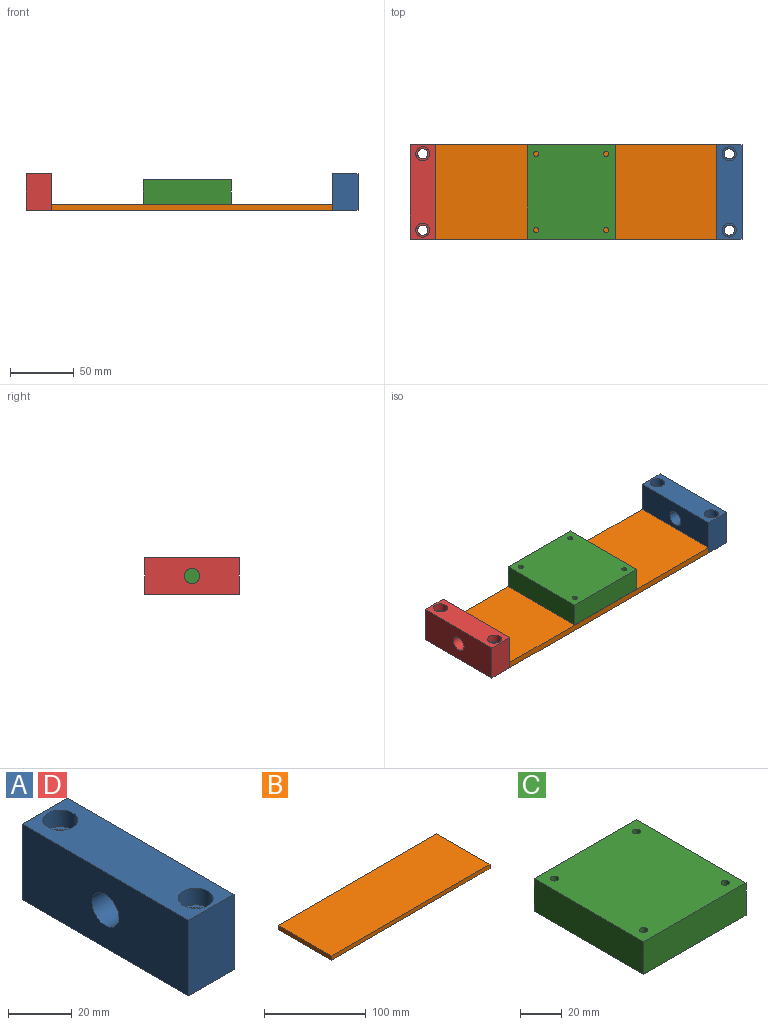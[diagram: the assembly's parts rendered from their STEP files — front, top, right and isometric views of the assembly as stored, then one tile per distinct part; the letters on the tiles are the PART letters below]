
ASSEMBLY  parts=4 mates=8
PART A: 13 faces, bbox 20x74x29 mm
  f0: cylinder r=4mm len=22.6mm, axis (0,0,1), area 568mm2, adj f3,f12
  f1: cylinder r=4mm len=22.6mm, axis (0,0,1), area 568mm2, adj f3,f9
  f2: plane 74x20mm, normal (0,0,1), area 1289.9mm2, adj f4,f5,f6,f7,f10,f11
  f3: plane 74x20mm, normal (0,0,-1), area 1379.5mm2, adj f0,f1,f4,f5,f6,f7
  f4: plane 74x29mm, normal (1,0,0), area 2032.9mm2, adj f2,f3,f5,f7,f8
  f5: plane 29x20mm, normal (0,1,0), area 580mm2, adj f2,f3,f4,f6
  f6: plane 74x29mm, normal (-1,0,0), area 2032.9mm2, adj f2,f3,f5,f7,f8
  f7: plane 29x20mm, normal (0,-1,0), area 580mm2, adj f2,f3,f4,f6
  f8: cylinder r=6mm len=20mm, axis (1,0,0), area 754mm2, adj f4,f6
  f9: plane 11x11mm, normal (0,0,1), area 44.8mm2, adj f1,f10
  f10: cylinder r=5.5mm len=11mm, axis (0,0,1), area 221.2mm2, adj f2,f9
  f11: cylinder r=5.5mm len=11mm, axis (0,0,1), area 221.2mm2, adj f2,f12
  f12: plane 11x11mm, normal (0,0,1), area 44.8mm2, adj f0,f11
PART B: 6 faces, bbox 221x74x5 mm
  f0: plane 74x5mm, normal (1,0,0), area 370mm2, adj f1,f3,f4,f5
  f1: plane 221x5mm, normal (0,1,0), area 1105mm2, adj f0,f2,f4,f5
  f2: plane 74x5mm, normal (-1,0,0), area 370mm2, adj f1,f3,f4,f5
  f3: plane 221x5mm, normal (0,-1,0), area 1105mm2, adj f0,f2,f4,f5
  f4: plane 221x74mm, normal (0,0,1), area 16354mm2, adj f0,f1,f2,f3
  f5: plane 221x74mm, normal (0,0,-1), area 16354mm2, adj f0,f1,f2,f3
PART C: 10 faces, bbox 69x74x19 mm
  f0: plane 74x69mm, normal (0,0,1), area 5055.7mm2, adj f2,f3,f4,f5,f6,f7,f8,f9
  f1: plane 74x69mm, normal (0,0,-1), area 5055.7mm2, adj f2,f3,f4,f5,f6,f7,f8,f9
  f2: plane 74x19mm, normal (1,0,0), area 1406mm2, adj f0,f1,f3,f5
  f3: plane 69x19mm, normal (0,1,0), area 1311mm2, adj f0,f1,f2,f4
  f4: plane 74x19mm, normal (-1,0,0), area 1406mm2, adj f0,f1,f3,f5
  f5: plane 69x19mm, normal (0,-1,0), area 1311mm2, adj f0,f1,f2,f4
  f6: cylinder r=2mm len=19mm, axis (0,0,1), area 238.8mm2, adj f0,f1
  f7: cylinder r=2mm len=19mm, axis (0,0,1), area 238.8mm2, adj f0,f1
  f8: cylinder r=2mm len=19mm, axis (0,0,1), area 238.8mm2, adj f0,f1
  f9: cylinder r=2mm len=19mm, axis (0,0,1), area 238.8mm2, adj f0,f1
PART D: same geometry as A
PLACE A t=(125.69,3.52,-1.71)mm
PLACE B t=(5.19,3.52,-1.71)mm fixed
PLACE C t=(1.4,3.52,3.29)mm
PLACE D t=(-115.31,3.52,-1.71)mm
MATE planar A.f3 <-> B.f5  axis (0,0,-1) through (125.69,3.52,-1.71)mm
MATE planar C.f3 <-> B.f1  axis (0,1,0) through (1.4,40.52,12.79)mm
MATE planar D.f3 <-> B.f5  axis (0,0,-1) through (-115.31,3.52,-1.71)mm
MATE planar D.f4 <-> B.f2  axis (1,0,0) through (-105.31,3.52,-1.71)mm
MATE planar C.f1 <-> B.f4  axis (0,0,-1) through (1.4,3.52,3.29)mm
MATE planar A.f5 <-> B.f1  axis (0,1,0) through (125.69,40.52,12.79)mm
MATE planar A.f6 <-> B.f0  axis (-1,0,0) through (115.69,3.52,-1.71)mm
MATE planar B.f1 <-> D.f5  axis (0,1,0) through (5.19,40.52,0.79)mm
